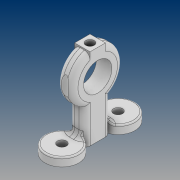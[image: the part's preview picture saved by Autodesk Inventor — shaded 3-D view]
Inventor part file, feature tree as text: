
AUTODESK INVENTOR PART (.ipt)
format: ipt  version: 2021 (Build 250183000, 183)  size: 339,968 bytes
history: native  units: mm
features: sketch x5, extrude x4, fillet x3, projected_geometry x2, hole x1, plane x1
ambient origin geometry x8: Origin, YZ Plane, XZ Plane, XY Plane, X Axis, Y Axis, Z Axis, Center Point
bodies: Solid1 (feature_tree)
feature tree (16):
  extrude  "Extrusion1"  Depth=12.0mm
  extrude  "Extrusion2"  Depth=3.0mm TaperAngle=0.0deg
  hole  "Hole1"  [1 undecoded]
  fillet  "Fillet1"  Radius=4.0mm
  plane  "Work Plane1"
  extrude  "Extrusion3"  Depth=2.0mm
  extrude  "Extrusion4"  Depth=5.5mm
  fillet  "Fillet2"  Radius=2.0mm
  fillet  "Fillet3"  Radius=3.0mm
  sketch  "Sketch1"  dims[d0=20.0mm d1=12.0mm]
  sketch  "Sketch2"  dims[d2=5.5mm d3=3.0mm d4=0.0mm]
  projected_geometry  "Projected Loop1"
  sketch  "Sketch3"  dims[d5=10.1mm d6=20.0mm d7=4.0mm]
  projected_geometry  "Projected Loop2"
  sketch  "Sketch4"  dims[d9=5.5mm d10=0.0mm]
  sketch  "Sketch5"  dims[d11=3.2mm d12=6.0mm d13=4.0mm d14=2.0mm d15=90.0deg d16=8.0mm d17=20.594885mm d18=2.0mm d19=5.5mm d21=2.0mm d22=0.0mm d23=3.0mm d24=7.75mm d25=0.0mm d26=2.0mm d27=0.5mm]
note: 1 required parameter value undecoded (feature->parameter linkage not recoverable at this tier; creation-order binding heuristic only, values carry confidence <= 0.55)
